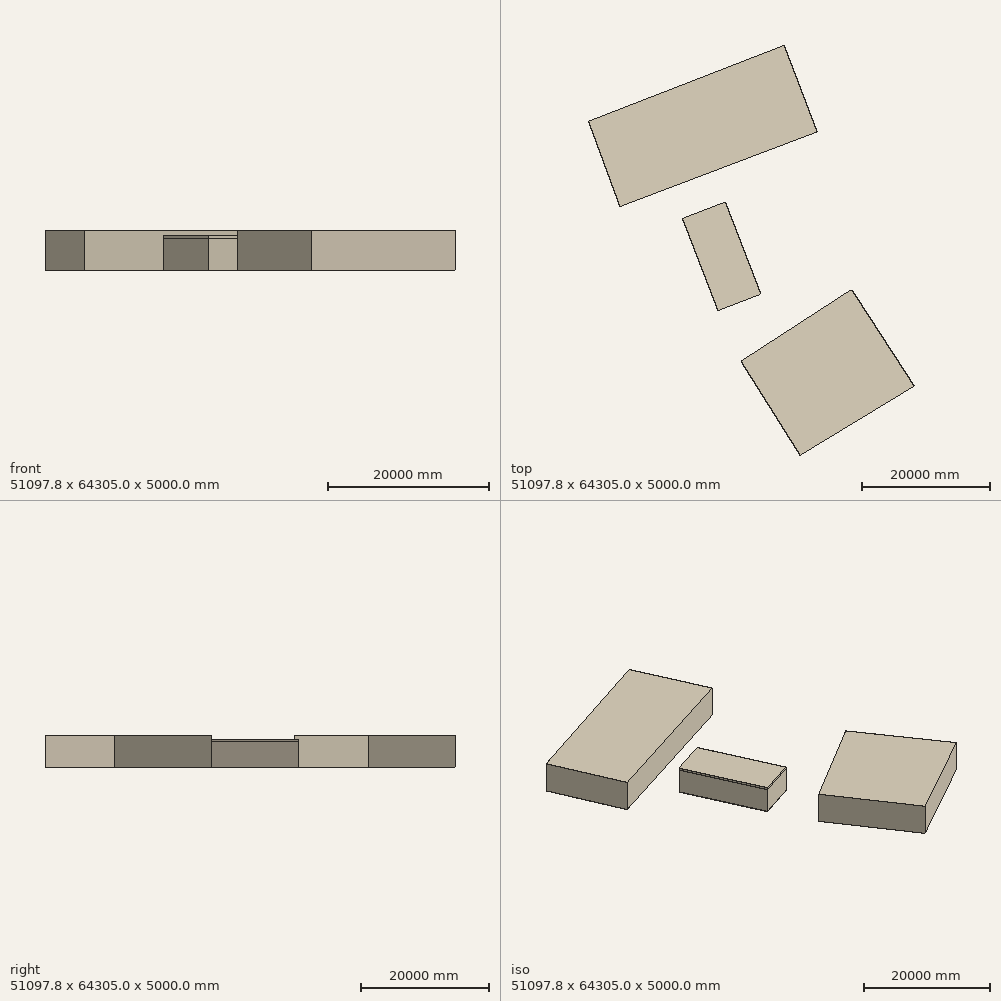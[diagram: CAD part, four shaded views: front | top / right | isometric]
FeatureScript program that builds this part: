
annotation { "Feature Type Name" : "Feature", "Feature Type Description" : "" }
export const myFeature = defineFeature(function(context is Context, id is Id, definition is map)
    precondition{}
    {
        {
            var Q0;
            Q0=qCreatedBy(makeId("Top.planeOp"),FACE);
            var sketch = newSketch(context, id + "F0", { "sketchPlane" : qUnion([Q0])});
            skLineSegment(sketch, "E0", {"start": v(-10158.18, -131.88) * mm, "end": v(9841.82, -131.88) * mm});
            skLineSegment(sketch, "E1", {"start": v(187539.75, 81737.34) * mm, "end": v(193121.23, 67288.97) * mm});
            skLineSegment(sketch, "E2", {"start": v(193121.23, 67288.97) * mm, "end": v(199849.27, 69888.05) * mm});
            skLineSegment(sketch, "E3", {"start": v(199849.27, 69888.05) * mm, "end": v(194267.79, 84336.42) * mm});
            skLineSegment(sketch, "E4", {"start": v(194267.79, 84336.42) * mm, "end": v(187539.75, 81737.34) * mm});
            skLineSegment(sketch, "E5", {"start": v(208669.68, 95326.9) * mm, "end": v(177736.31, 83607) * mm});
            skLineSegment(sketch, "E6", {"start": v(177736.31, 83607) * mm, "end": v(172814.6, 96986.59) * mm});
            skLineSegment(sketch, "E7", {"start": v(172814.6, 96986.59) * mm, "end": v(203493.68, 108899.4) * mm});
            skLineSegment(sketch, "E8", {"start": v(203493.68, 108899.4) * mm, "end": v(208669.68, 95326.9) * mm});
            skLineSegment(sketch, "E9", {"start": v(175795.11, 83973.93) * mm, "end": v(183542.53, 63918.76) * mm, "construction": true});
            skLineSegment(sketch, "E10", {"start": v(180970.64, 84832.4) * mm, "end": v(187893.07, 65474.8) * mm, "construction": true});
            skLineSegment(sketch, "E11", {"start": v(170830.15, 81002.61) * mm, "end": v(178579.4, 61691.7) * mm, "construction": true});
            skLineSegment(sketch, "E12", {"start": v(193121.23, 67288.97) * mm, "end": v(194231.34, 63706.36) * mm, "construction": true});
            skLineSegment(sketch, "E13", {"start": v(194231.34, 63706.36) * mm, "end": v(179655.72, 58700.32) * mm, "construction": true});
            skLineSegment(sketch, "E14", {"start": v(179655.72, 58700.32) * mm, "end": v(178466.66, 61613.23) * mm, "construction": true});
            skLineSegment(sketch, "E15", {"start": v(178466.66, 61613.23) * mm, "end": v(178579.4, 61691.7) * mm, "construction": true});
            skLineSegment(sketch, "E16", {"start": v(196729.08, 59349.96) * mm, "end": v(214079.01, 70606.48) * mm});
            skLineSegment(sketch, "E17", {"start": v(214079.01, 70606.48) * mm, "end": v(223912.44, 55450) * mm});
            skLineSegment(sketch, "E18", {"start": v(223912.44, 55450) * mm, "end": v(206013.89, 44594.36) * mm});
            skLineSegment(sketch, "E19", {"start": v(206013.89, 44594.36) * mm, "end": v(196729.08, 59349.96) * mm});
            skLineSegment(sketch, "E20", {"start": v(208670.5, 45709.94) * mm, "end": v(190801.62, 34997.4) * mm, "construction": true});
            skLineSegment(sketch, "E21", {"start": v(190801.62, 34997.4) * mm, "end": v(178771.96, 39826.82) * mm, "construction": true});
            skLineSegment(sketch, "E22", {"start": v(178771.96, 39826.82) * mm, "end": v(151260.15, 102166) * mm, "construction": true});
            skLineSegment(sketch, "E23", {"start": v(151260.15, 102166) * mm, "end": v(156670.24, 107744.42) * mm, "construction": true});
            skLineSegment(sketch, "E24", {"start": v(156670.24, 107744.42) * mm, "end": v(159799.36, 111734.04) * mm, "construction": true});
            skLineSegment(sketch, "E25", {"start": v(159799.36, 111734.04) * mm, "end": v(161481.26, 114667.59) * mm, "construction": true});
            skLineSegment(sketch, "E26", {"start": v(161481.26, 114667.59) * mm, "end": v(163124.04, 117483.79) * mm, "construction": true});
            skLineSegment(sketch, "E27", {"start": v(163124.04, 117483.79) * mm, "end": v(164917, 120674.92) * mm, "construction": true});
            skLineSegment(sketch, "E28", {"start": v(164917, 120674.92) * mm, "end": v(164917, 123686.68) * mm, "construction": true});
            skLineSegment(sketch, "E29", {"start": v(164917, 123686.68) * mm, "end": v(164643.2, 124762.32) * mm, "construction": true});
            skLineSegment(sketch, "E30", {"start": v(164643.2, 124762.32) * mm, "end": v(164643.2, 127206.94) * mm, "construction": true});
            skLineSegment(sketch, "E31", {"start": v(164643.2, 127206.94) * mm, "end": v(167061.37, 131699.1) * mm, "construction": true});
            skLineSegment(sketch, "E32", {"start": v(167061.37, 131699.1) * mm, "end": v(174739.8, 134962.66) * mm, "construction": true});
            skLineSegment(sketch, "E33", {"start": v(174739.8, 134962.66) * mm, "end": v(189157.47, 141112.01) * mm, "construction": true});
            skLineSegment(sketch, "E34", {"start": v(189157.47, 141112.01) * mm, "end": v(191512.92, 135589.46) * mm, "construction": true});
            skLineSegment(sketch, "E35", {"start": v(191512.92, 135589.46) * mm, "end": v(190598.55, 135199.47) * mm, "construction": true});
            skLineSegment(sketch, "E36", {"start": v(190598.55, 135199.47) * mm, "end": v(201688.16, 110933.7) * mm, "construction": true});
            skLineSegment(sketch, "E37", {"start": v(201688.16, 110933.7) * mm, "end": v(202729.39, 108955.99) * mm, "construction": true});
            skLineSegment(sketch, "E38", {"start": v(202729.39, 108955.99) * mm, "end": v(203642.8, 109310.67) * mm, "construction": true});
            skLineSegment(sketch, "E39", {"start": v(203642.8, 109310.67) * mm, "end": v(209361.07, 95181.4) * mm, "construction": true});
            skLineSegment(sketch, "E40", {"start": v(209361.07, 95181.4) * mm, "end": v(209730.67, 93234.83) * mm, "construction": true});
            skLineSegment(sketch, "E41", {"start": v(209730.67, 93234.83) * mm, "end": v(208728.07, 92845.51) * mm, "construction": true});
            skLineSegment(sketch, "E42", {"start": v(208728.07, 92845.51) * mm, "end": v(217027.5, 72191.76) * mm, "construction": true});
            skLineSegment(sketch, "E43", {"start": v(217027.5, 72191.76) * mm, "end": v(214271.76, 70679.21) * mm, "construction": true});
            skLineSegment(sketch, "E44", {"start": v(214271.76, 70679.21) * mm, "end": v(224345.41, 55221.25) * mm, "construction": true});
            skLineSegment(sketch, "E45", {"start": v(224345.41, 55221.25) * mm, "end": v(208670.5, 45709.94) * mm, "construction": true});
            skLineSegment(sketch, "E46", {"start": v(187539.75, 81737.34) * mm, "end": v(185689.7, 86620.34) * mm});
            skLineSegment(sketch, "E47", {"start": v(194267.79, 84336.42) * mm, "end": v(192434.3, 89175.7) * mm});
            skSolve(sketch);
        }
        {
            var Q0;
            Q0=makeQuery(id+"F0.imprint","IMPRINT",FACE,{"disambiguationData":[TD([[makeQuery(id+"F0.imprint","IMPRINT",EDGE,{"derivedFrom":sQuery(id+"F0.wireOp",EDGE,"E1")}),1.0]])]});
            extrude(context, id + "F1", {"entities" : qUnion([Q0]), "depth" : 50 * mm, "offsetDistance" : 25 * mm});
        }
        {
            var Q0;
            Q0=makeQuery(id+"F1.opExtrude","CAP_FACE",FACE,{"disambiguationData":[OSD([sQuery(id+"F0.wireOp",EDGE,"E1"),sQuery(id+"F0.wireOp",EDGE,"E2"),sQuery(id+"F0.wireOp",EDGE,"E3"),sQuery(id+"F0.wireOp",EDGE,"E4")])],"isStart":false});
            var sketch = newSketch(context, id + "F2", { "sketchPlane" : qUnion([Q0])});
            skLineSegment(sketch, "E48", {"start": v(194267.79, 84336.42) * mm, "end": v(199849.27, 69888.05) * mm});
            skLineSegment(sketch, "E49", {"start": v(199849.27, 69888.05) * mm, "end": v(193121.23, 67288.97) * mm});
            skLineSegment(sketch, "E50", {"start": v(193121.23, 67288.97) * mm, "end": v(187539.75, 81737.34) * mm});
            skLineSegment(sketch, "E51", {"start": v(187539.75, 81737.34) * mm, "end": v(194267.79, 84336.42) * mm});
            skLineSegment(sketch, "E52.0", {"start": v(193327.32, 67754.52) * mm, "end": v(188005.29, 81531.26) * mm});
            skLineSegment(sketch, "E52.1", {"start": v(199383.73, 70094.14) * mm, "end": v(193327.32, 67754.52) * mm});
            skLineSegment(sketch, "E52.2", {"start": v(194061.7, 83870.88) * mm, "end": v(199383.73, 70094.14) * mm});
            skLineSegment(sketch, "E52.3", {"start": v(188005.29, 81531.26) * mm, "end": v(194061.7, 83870.88) * mm});
            skLineSegment(sketch, "E53", {"start": v(195186, 80960.5) * mm, "end": v(189129.59, 78620.87) * mm});
            skLineSegment(sketch, "E54.0", {"start": v(195142.76, 81072.43) * mm, "end": v(189086.35, 78732.8) * mm});
            skLineSegment(sketch, "E55", {"start": v(192251.03, 79955.34) * mm, "end": v(191169.97, 82753.79) * mm});
            skLineSegment(sketch, "E56.0", {"start": v(192139.09, 79912.1) * mm, "end": v(191058.03, 82710.55) * mm});
            skSolve(sketch);
        }
        {
            var Q0;
            Q0=makeQuery(id+"F2.imprint","IMPRINT",FACE,{"disambiguationData":[TD([[makeQuery(id+"F2.imprint","IMPRINT",EDGE,{"derivedFrom":sQuery(id+"F2.wireOp",EDGE,"E48")}),1.0]])]});
            extrude(context, id + "F3", {"entities" : qUnion([Q0]), "depth" : 4000 * mm, "offsetDistance" : 25 * mm});
        }
        {
            var Q0;
            Q0=makeQuery(id+"F3.opExtrude","CAP_FACE",FACE,{"disambiguationData":[OSD([sQuery(id+"F2.wireOp",EDGE,"E48"),sQuery(id+"F2.wireOp",EDGE,"E49"),sQuery(id+"F2.wireOp",EDGE,"E50"),sQuery(id+"F2.wireOp",EDGE,"E51"),sQuery(id+"F2.wireOp",EDGE,"E52.0"),sQuery(id+"F2.wireOp",EDGE,"E52.1"),sQuery(id+"F2.wireOp",EDGE,"E52.2"),sQuery(id+"F2.wireOp",EDGE,"E52.3")])],"isStart":false});
            var sketch = newSketch(context, id + "F4", { "sketchPlane" : qUnion([Q0])});
            skLineSegment(sketch, "E57", {"start": v(187539.75, 81737.34) * mm, "end": v(194267.79, 84336.42) * mm});
            skLineSegment(sketch, "E58", {"start": v(194267.79, 84336.42) * mm, "end": v(199849.27, 69888.05) * mm});
            skLineSegment(sketch, "E59", {"start": v(199849.27, 69888.05) * mm, "end": v(193121.23, 67288.97) * mm});
            skLineSegment(sketch, "E60", {"start": v(193121.23, 67288.97) * mm, "end": v(187539.75, 81737.34) * mm});
            skSolve(sketch);
        }
        {
            var Q0;
            Q0=qSketchRegion(id+"F4",true);
            extrude(context, id + "F5", {"entities" : qUnion([Q0]), "depth" : 360 * mm, "offsetDistance" : 25 * mm});
        }
        {
            var Q0;
            Q0=makeQuery(id+"F3.opExtrude","SWEPT_FACE",FACE,{"disambiguationData":[OSD([sQuery(id+"F2.wireOp",EDGE,"E51")])]});
            var sketch = newSketch(context, id + "F6", { "sketchPlane" : qUnion([Q0])});
            skLineSegment(sketch, "E61.bottom", {"start": v(-205994.37, 2050) * mm, "end": v(-204994.37, 2050) * mm});
            skLineSegment(sketch, "E61.top", {"start": v(-205994.37, 50) * mm, "end": v(-204994.37, 50) * mm});
            skLineSegment(sketch, "E61.left", {"start": v(-205994.37, 2050) * mm, "end": v(-205994.37, 50) * mm});
            skLineSegment(sketch, "E61.right", {"start": v(-204994.37, 2050) * mm, "end": v(-204994.37, 50) * mm});
            skSolve(sketch);
        }
        {
            var Q0;
            Q0=qSketchRegion(id+"F6",true);
            extrude(context, id + "F7", {"entities" : qUnion([Q0]), "operationType" : NewBodyOperationType.REMOVE, "oppositeDirection" : true, "depth" : 360 * mm, "offsetDistance" : 25 * mm});
        }
        {
            var Q0;
            {var subQ0=sQuery(id+"F2.wireOp",EDGE,"E53");Q0=makeQuery(id+"F2.imprint","IMPRINT",FACE,{"disambiguationData":[TD([[makeQuery(id+"F2.imprint","IMPRINT",EDGE,{"derivedFrom":subQ0}),-1.0]])]});}
            var Q1;
            {var subQ0=sQuery(id+"F2.wireOp",EDGE,"E55");Q1=makeQuery(id+"F2.imprint","IMPRINT",FACE,{"disambiguationData":[TD([[makeQuery(id+"F2.imprint","IMPRINT",EDGE,{"derivedFrom":subQ0}),1.0]])]});}
            extrude(context, id + "F8", {"entities" : qUnion([Q0, Q1]), "depth" : 2400 * mm, "offsetDistance" : 25 * mm});
        }
        {
            var Q0;
            Q0=makeQuery(id+"F8.opExtrude","CAP_FACE",FACE,{"disambiguationData":[OSD([sQuery(id+"F2.wireOp",EDGE,"E52.0"),sQuery(id+"F2.wireOp",EDGE,"E52.2"),sQuery(id+"F2.wireOp",EDGE,"E53"),sQuery(id+"F2.wireOp",EDGE,"E54.0")])],"isStart":false});
            var sketch = newSketch(context, id + "F9", { "sketchPlane" : qUnion([Q0])});
            skLineSegment(sketch, "E62", {"start": v(195186, 80960.5) * mm, "end": v(189129.59, 78620.87) * mm});
            skLineSegment(sketch, "E63", {"start": v(195186, 80960.5) * mm, "end": v(194061.7, 83870.88) * mm});
            skLineSegment(sketch, "E64", {"start": v(194061.7, 83870.88) * mm, "end": v(188005.29, 81531.26) * mm});
            skLineSegment(sketch, "E65", {"start": v(188005.29, 81531.26) * mm, "end": v(189129.59, 78620.87) * mm});
            skSolve(sketch);
        }
        {
            var Q0;
            Q0=qSketchRegion(id+"F9",true);
            extrude(context, id + "F10", {"entities" : qUnion([Q0]), "depth" : 200 * mm, "offsetDistance" : 25 * mm});
        }
        {
            var Q0;
            Q0=makeQuery(id+"F8.opExtrude","SWEPT_FACE",FACE,{"disambiguationData":[OSD([sQuery(id+"F2.wireOp",EDGE,"E53")])]});
            var sketch = newSketch(context, id + "F11", { "sketchPlane" : qUnion([Q0])});
            skLineSegment(sketch, "E66.bottom", {"start": v(205054.37, 50) * mm, "end": v(206054.37, 50) * mm});
            skLineSegment(sketch, "E66.top", {"start": v(205054.37, 2050) * mm, "end": v(206054.37, 2050) * mm});
            skLineSegment(sketch, "E66.left", {"start": v(205054.37, 50) * mm, "end": v(205054.37, 2050) * mm});
            skLineSegment(sketch, "E66.right", {"start": v(206054.37, 50) * mm, "end": v(206054.37, 2050) * mm});
            skLineSegment(sketch, "E67.bottom", {"start": v(209446.98, 50) * mm, "end": v(208446.98, 50) * mm});
            skLineSegment(sketch, "E67.top", {"start": v(209446.98, 2050) * mm, "end": v(208446.98, 2050) * mm});
            skLineSegment(sketch, "E67.left", {"start": v(209446.98, 50) * mm, "end": v(209446.98, 2050) * mm});
            skLineSegment(sketch, "E67.right", {"start": v(208446.98, 50) * mm, "end": v(208446.98, 2050) * mm});
            skSolve(sketch);
        }
        {
            var Q0;
            Q0=qSketchRegion(id+"F11",true);
            extrude(context, id + "F12", {"entities" : qUnion([Q0]), "operationType" : NewBodyOperationType.REMOVE, "oppositeDirection" : true, "depth" : 120 * mm, "offsetDistance" : 25 * mm});
        }
        {
            var Q0;
            Q0=makeQuery(id+"F0.imprint","IMPRINT",FACE,{"disambiguationData":[TD([[makeQuery(id+"F0.imprint","IMPRINT",EDGE,{"derivedFrom":sQuery(id+"F0.wireOp",EDGE,"E16")}),-1.0]])]});
            extrude(context, id + "F13", {"entities" : qUnion([Q0]), "depth" : 5000 * mm, "offsetDistance" : 25 * mm});
        }
        {
            var Q0;
            {var subQ0=sQuery(id+"F0.wireOp",EDGE,"E6");Q0=makeQuery(id+"F0.imprint","IMPRINT",FACE,{"disambiguationData":[TD([[makeQuery(id+"F0.imprint","IMPRINT",EDGE,{"derivedFrom":subQ0}),-1.0]])]});}
            extrude(context, id + "F14", {"entities" : qUnion([Q0]), "depth" : 5000 * mm, "offsetDistance" : 25 * mm});
        }
    });
